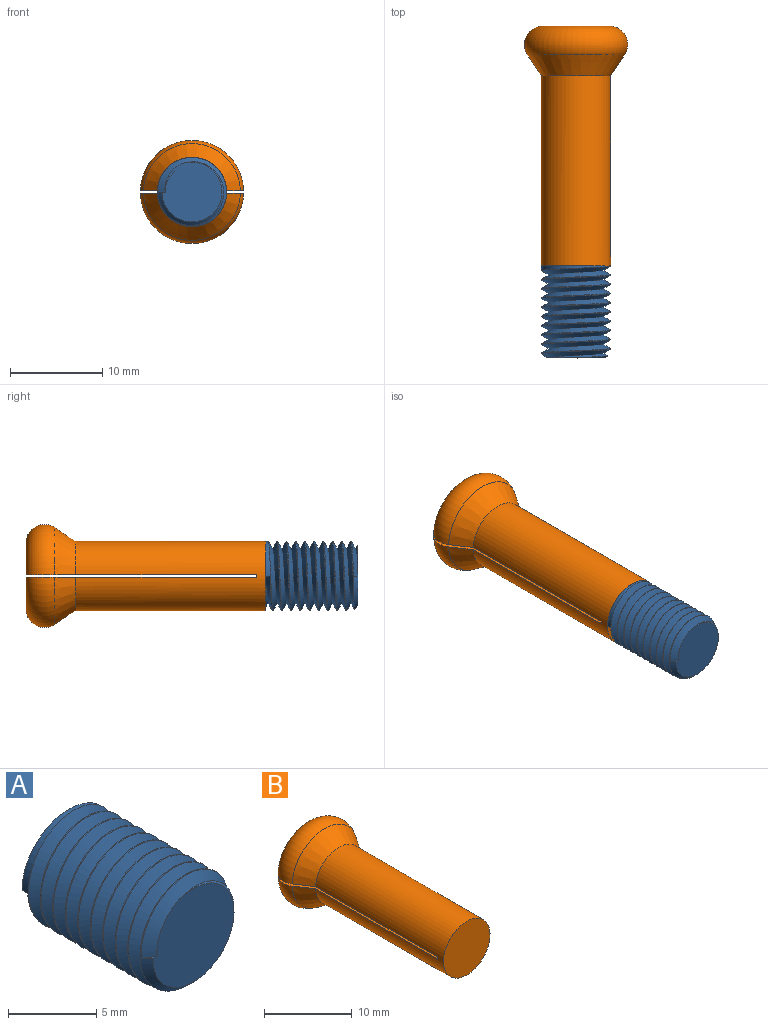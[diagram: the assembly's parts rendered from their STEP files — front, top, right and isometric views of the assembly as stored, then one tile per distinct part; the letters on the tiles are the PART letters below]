
ASSEMBLY  parts=2 mates=1
PART A: 8 faces, bbox 7.6x11x8.8 mm
  f0: cylinder r=3.75mm len=9.5mm, axis (0,1,0), area 12.9mm2, adj f2,f3,f4,f5,f7
  f1: plane 6.6x6.6mm, normal (0,-1,0), area 32.6mm2, adj f3,f5,f6,f7
  f2: plane 7.5x7.13mm, normal (0,1,0), area 40mm2, adj f0,f4,f5
  f3: cone r=3.25mm half-angle=45deg, axis (0,1,0), area 6.5mm2, adj f0,f1,f5,f6,f7
  f4: plane 0.83x0.47mm, normal (0,0,-1), area 0.2mm2, adj f0,f2,f5,f7
  f5: bspline ~10.47x8.66mm, area 194.2mm2, adj f0,f1,f2,f3,f4,f6,f7
  f6: plane 0.75x0.43mm, normal (0,0,1), area 0.1mm2, adj f1,f3,f5
  f7: bspline ~10.47x7.5mm, area 190.9mm2, adj f0,f1,f3,f4,f5
PART B: 17 faces, bbox 12.1x26x12.1 mm
  f0: cone r=3.67mm half-angle=33.8deg, axis (0,1,0), area 37.5mm2, adj f1,f4,f11,f13
  f1: torus R=3.58mm, axis (0,-1,0), area 65.6mm2, adj f0,f2,f11,f13
  f2: cylinder r=3.75mm len=7.49mm, axis (0,1,0), area 0.1mm2, adj f1,f8,f11,f13
  f3: cylinder r=3.75mm len=7.49mm, axis (0,1,0), area 0.1mm2, adj f5,f12,f14,f16
  f4: cylinder r=3.75mm len=20.62mm, axis (0,1,0), area 474mm2, adj f0,f7,f10,f11,f12,f13,f14,f15
  f5: plane 7.49x3.6mm, normal (0,1,0), area 19.7mm2, adj f3,f9,f12,f14
  f6: cylinder r=1mm len=25mm, axis (0,1,0), area 71mm2, adj f8,f10,f11,f13
  f7: plane 7.5x7.5mm, normal (0,-1,0), area 44.2mm2, adj f4
  f8: plane 7.49x3.6mm, normal (0,1,0), area 19.7mm2, adj f2,f6,f11,f13
  f9: cylinder r=1mm len=25mm, axis (0,1,0), area 71mm2, adj f5,f10,f12,f14
  f10: plane 7.5x2mm, normal (0,1,0), area 4.8mm2, adj f4,f6,f9,f11,f12,f13,f14
  f11: plane 25.01x4.61mm, normal (0,0,-1), area 75.4mm2, adj f0,f1,f2,f4,f6,f8,f10
  f12: plane 25.01x4.61mm, normal (0,0,1), area 75.4mm2, adj f3,f4,f5,f9,f10,f15,f16
  f13: plane 25.01x4.61mm, normal (0,0,-1), area 75.4mm2, adj f0,f1,f2,f4,f6,f8,f10
  f14: plane 25.01x4.61mm, normal (0,0,1), area 75.4mm2, adj f3,f4,f5,f9,f10,f15,f16
  f15: cone r=3.67mm half-angle=33.8deg, axis (0,1,0), area 37.5mm2, adj f4,f12,f14,f16
  f16: torus R=3.58mm, axis (0,-1,0), area 65.6mm2, adj f3,f12,f14,f15
PLACE A t=(-2.18,-20.13,9.14)mm
PLACE B rot(axis=(0,-0.99,-0.12),0deg) t=(-2.18,5.87,9.14)mm
MATE revolute B.f2 <-> A.f0  axis (0,-1,0) through (-2.18,-20.13,9.14)mm
